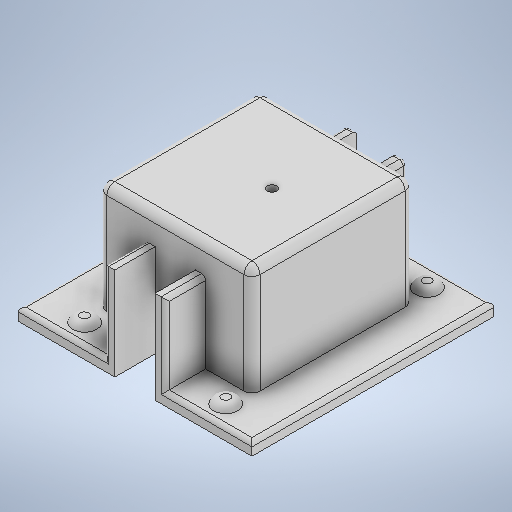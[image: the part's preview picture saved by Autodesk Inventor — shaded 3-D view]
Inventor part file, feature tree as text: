
AUTODESK INVENTOR PART (.ipt)
format: ipt  version: 2025.2 (Build 292293000, 293)  size: 474,112 bytes
history: native  units: mm
features: extrude x14, sketch x14, plane x3, fillet x3
ambient origin geometry x8: Origin, YZ Plane, XZ Plane, XY Plane, X Axis, Y Axis, Z Axis, Center Point
bodies: Body1 (feature_tree)
feature tree (34):
  plane  "Work Plane5"
  extrude  "Extrusion34"  Depth=40.0mm
  plane  "Work Plane2"
  extrude  "Extrusion35"  Depth=30.0mm
  plane  "Work Plane1"
  extrude  "Extrusion51"  Depth=30.0mm
  sketch  "Sketch77"  dims[d211=10.0mm d212=0.0mm d219=35.0mm]
  extrude  "Extrusion53"  Depth=10.0mm
  extrude  "Extrusion54"  Depth=60.0mm
  extrude  "Extrusion56"  Depth=3.0mm TaperAngle=0.0deg
  extrude  "Extrusion58"  Depth=11.5mm
  extrude  "Extrusion59"  Depth=5.4mm
  extrude  "Extrusion60"  Depth=30.0mm TaperAngle=0.0deg
  extrude  "Extrusion61"  Depth=10.0mm
  extrude  "Extrusion62"  Depth=20.0mm TaperAngle=0.0deg
  extrude  "Extrusion63"  Depth=10.0mm
  extrude  "Extrusion64"  Depth=10.0mm
  fillet  "Fillet1"  Radius=2.5mm
  fillet  "Fillet2"  Radius=2.5mm
  extrude  "Extrusion65"  Depth=4.2mm
  fillet  "Fillet3"  Radius=4.1mm
  sketch  "Sketch45"  dims[d142=38.0mm d143=40.0mm]
  sketch  "Sketch47"  dims[d144=30.0mm d145=0.0mm d146=36.0mm]
  sketch  "Sketch74"  dims[d147=30.0mm d148=-2.617994mm d210=2.3mm]
  sketch  "Sketch78"  dims[d220=58.0mm d221=60.0mm]
  sketch  "Sketch81"  dims[d222=3.0mm d223=0.0mm d224=3.0mm d225=0.0mm]
  sketch  "Sketch85"  dims[d232=5.0mm d233=11.5mm]
  sketch  "Sketch86"  dims[d236=5.4mm d243=5.4mm]
  sketch  "Sketch87"  dims[d247=5.4mm d250=30.0mm d251=0.0mm]
  sketch  "Sketch88"  dims[d256=15.0mm d257=10.0mm]
  sketch  "Sketch89"  dims[d258=15.0mm d259=20.0mm d260=0.0mm]
  sketch  "Sketch90"  dims[d261=10.0mm d262=10.0mm]
  sketch  "Sketch91"  dims[d263=10.0mm d264=10.0mm d265=2.5mm d266=2.5mm]
  sketch  "Sketch92"  dims[d267=23.5mm d268=0.0mm d269=4.2mm d270=4.1mm d271=40.25mm d272=0.0mm d273=8.0mm d274=1.5mm d275=0.0mm d276=8.0mm d277=1.5mm d278=0.0mm d279=10.0mm d280=4.5mm d281=5.7mm d282=0.0mm d283=10.0mm d284=4.5mm d285=5.7mm d286=0.0mm d287=12.5mm d288=12.5mm d289=1.0mm d290=2.0mm d291=6.0mm d292=6.0mm d293=6.0mm d294=6.0mm d295=1.5mm d296=0.0mm d297=2.0mm d49=0.5mm d50=0.872665mm d51=0.5mm d52=0.872665mm d130=0.5mm d131=0.872665mm d132=0.5mm d133=0.872665mm d156=0.5mm d157=0.872665mm d158=0.5mm d159=0.872665mm d173=0.5mm d174=0.872665mm d175=0.5mm d176=0.872665mm d226=0.5mm d227=0.872665mm]
